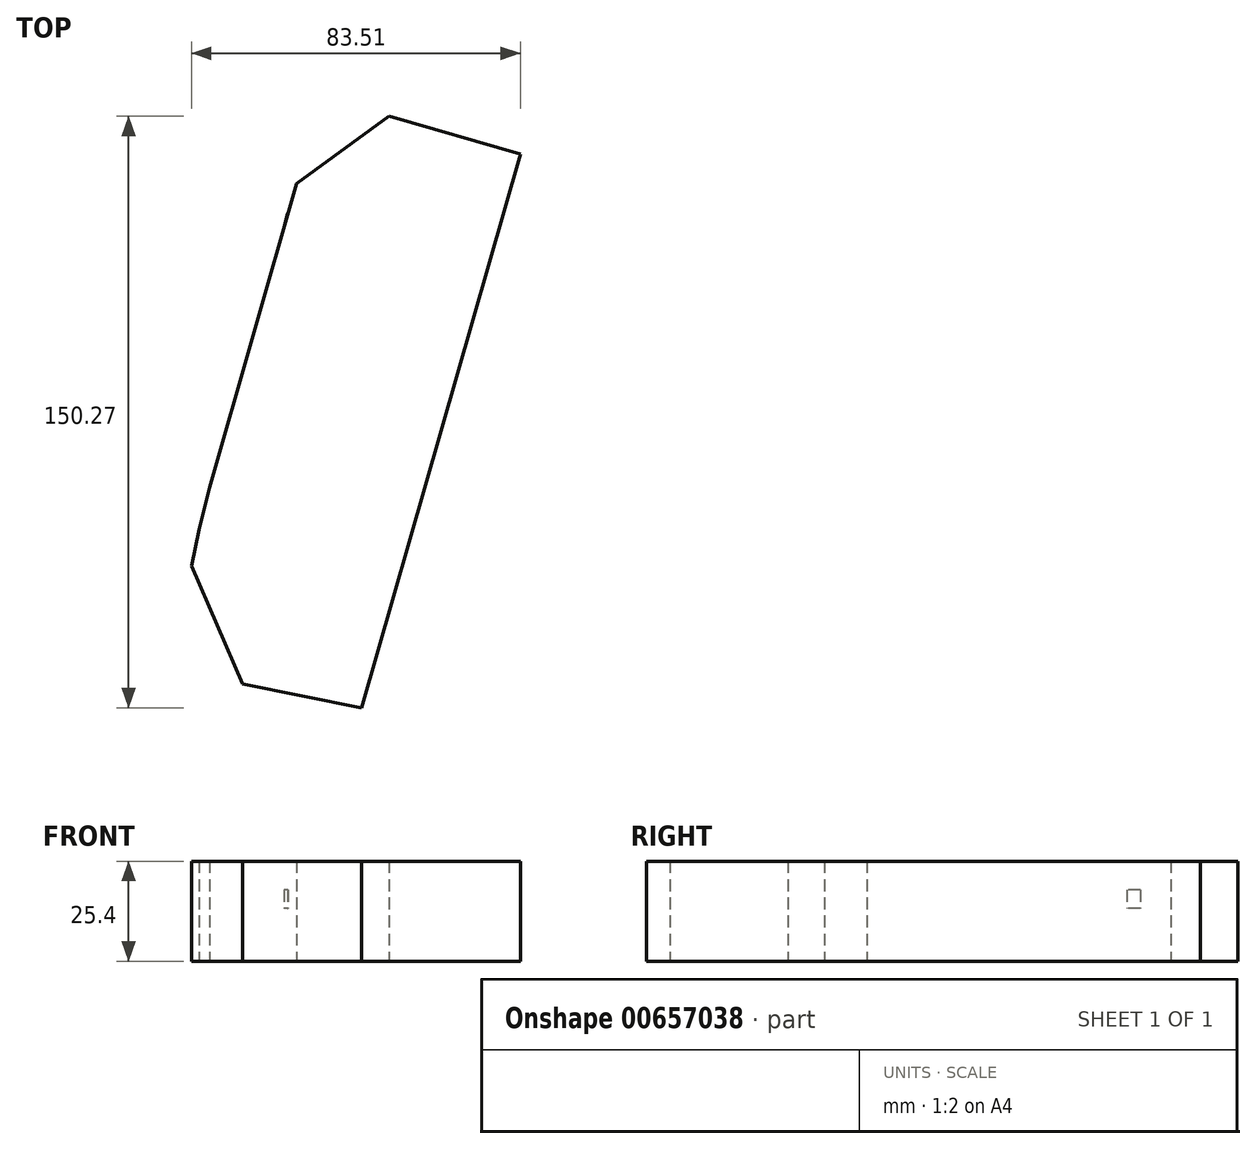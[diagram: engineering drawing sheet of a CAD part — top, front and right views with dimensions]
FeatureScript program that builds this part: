
annotation { "Feature Type Name" : "Feature", "Feature Type Description" : "" }
export const myFeature = defineFeature(function(context is Context, id is Id, definition is map)
    precondition{}
    {
        {
            var Q0;
            Q0=qCreatedBy(makeId("Top.planeOp"),FACE);
            var sketch = newSketch(context, id + "F0", { "sketchPlane" : qUnion([Q0])});
            skLineSegment(sketch, "E0", {"start": v(-48.83, 60.74) * mm, "end": v(-15.54, 51.2) * mm});
            skLineSegment(sketch, "E1", {"start": v(-15.54, 51.2) * mm, "end": v(-22.01, 28.6) * mm});
            skLineSegment(sketch, "E2", {"start": v(-22.01, 28.6) * mm, "end": v(-42, 34.34) * mm});
            skLineSegment(sketch, "E3", {"start": v(-22.01, 28.6) * mm, "end": v(-38.55, -29.09) * mm});
            skLineSegment(sketch, "E4", {"start": v(-48.83, 60.74) * mm, "end": v(-76.44, -49.94) * mm});
            skLineSegment(sketch, "E5", {"start": v(-38.55, -29.09) * mm, "end": v(-55.87, -89.53) * mm});
            skLineSegment(sketch, "E6", {"start": v(-76.44, -49.94) * mm, "end": v(-86.07, -83.52) * mm});
            skLineSegment(sketch, "E7", {"start": v(-86.07, -83.52) * mm, "end": v(-55.87, -89.53) * mm});
            skLineSegment(sketch, "E8", {"start": v(-86.07, -83.52) * mm, "end": v(-76.44, -85.43) * mm});
            skLineSegment(sketch, "E9", {"start": v(-76.44, -49.94) * mm, "end": v(-49.61, 57.6) * mm});
            skLineSegment(sketch, "E10", {"start": v(-49.61, 57.6) * mm, "end": v(-48.83, 60.74) * mm});
            skLineSegment(sketch, "E11", {"start": v(-48.83, 60.74) * mm, "end": v(-72.4, 43.7) * mm});
            skLineSegment(sketch, "E12", {"start": v(-72.4, 43.7) * mm, "end": v(-94.53, -33.52) * mm});
            skLineSegment(sketch, "E13", {"start": v(-94.53, -33.52) * mm, "end": v(-97.2, -44.24) * mm});
            skLineSegment(sketch, "E14", {"start": v(-97.2, -44.24) * mm, "end": v(-86.07, -83.52) * mm});
            skLineSegment(sketch, "E15", {"start": v(-97.2, -44.24) * mm, "end": v(-99.05, -53.54) * mm});
            skLineSegment(sketch, "E16", {"start": v(-99.05, -53.54) * mm, "end": v(-86.07, -83.52) * mm});
            skLineSegment(sketch, "E17", {"start": v(-92.56, -53.54) * mm, "end": v(-93.38, -57.7) * mm});
            skPoint(sketch, "E17.startSnap0", {"position": v(-92.56, -68.53) * mm});
            skSolve(sketch);
        }
        {
            var Q0;
            Q0 = qSketchRegion(id + "F0", true);
            extrude(context, id + "F1", {"entities" : qUnion([Q0]), "depth" : 25.4 * mm, "offsetDistance" : 25.4 * mm});
        }
        {
            var Q0;
            Q0=makeQuery(id+"F1.opExtrude","SWEPT_FACE",FACE,{"disambiguationData":[OSD([sQuery(id+"F0.wireOp",EDGE,"E12")])]});
            var sketch = newSketch(context, id + "F2", { "sketchPlane" : qUnion([Q0])});
            skLineSegment(sketch, "E18.bottom", {"start": v(-14.03, 18.09) * mm, "end": v(-10.52, 18.09) * mm});
            skLineSegment(sketch, "E18.top", {"start": v(-14.03, 13.45) * mm, "end": v(-10.52, 13.45) * mm});
            skLineSegment(sketch, "E18.left", {"start": v(-14.03, 18.09) * mm, "end": v(-14.03, 13.45) * mm});
            skLineSegment(sketch, "E18.right", {"start": v(-10.52, 18.09) * mm, "end": v(-10.52, 13.45) * mm});
            skSolve(sketch);
        }
        {
            var Q0;
            Q0 = qSketchRegion(id + "F2", true);
            extrude(context, id + "F3", {"entities" : qUnion([Q0]), "operationType" : NewBodyOperationType.ADD, "depth" : 0.03 * mm, "offsetDistance" : 25.4 * mm});
        }
    });
